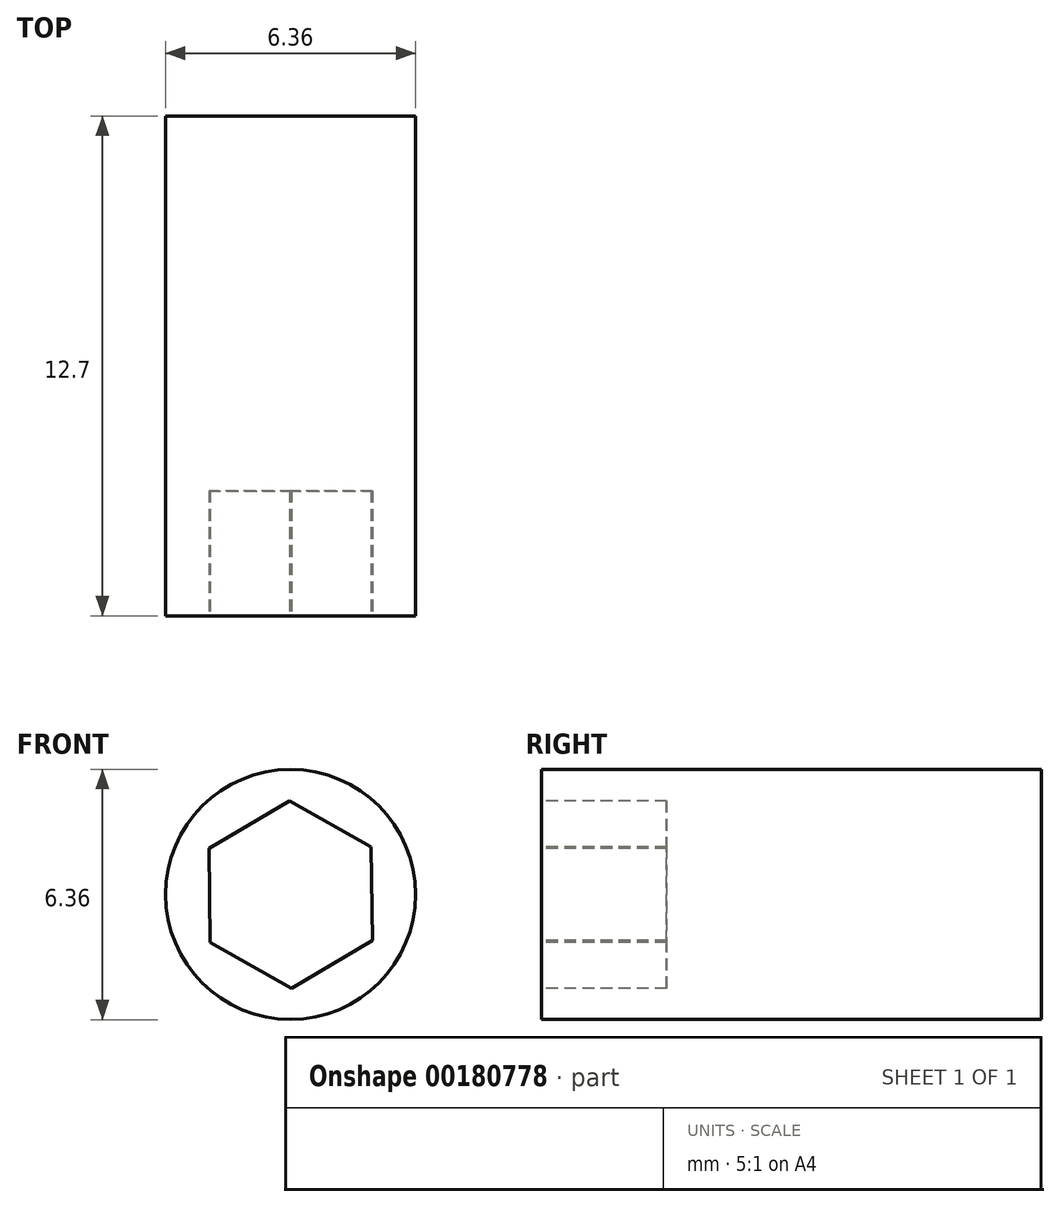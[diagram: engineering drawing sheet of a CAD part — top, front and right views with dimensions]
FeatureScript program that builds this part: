
annotation { "Feature Type Name" : "Feature", "Feature Type Description" : "" }
export const myFeature = defineFeature(function(context is Context, id is Id, definition is map)
    precondition{}
    {
        {
            var Q0;
            Q0=qCreatedBy(makeId("Front.planeOp"),FACE);
            var sketch = newSketch(context, id + "F0", { "sketchPlane" : qUnion([Q0])});
            skCircle(sketch, "E0", {"center": v(0, 0) * mm, "radius": 3.18 * mm});
            skSolve(sketch);
        }
        {
            var Q0;
            Q0 = qSketchRegion(id + "F0", true);
            extrude(context, id + "F1", {"entities" : qUnion([Q0]), "depth" : 12.7 * mm});
        }
        {
            var Q0;
            Q0=makeQuery(id+"F1.opExtrude","CAP_FACE",FACE,{"disambiguationData":[OSD([sQuery(id+"F0.wireOp",EDGE,"E0")])],"isStart":false});
            var sketch = newSketch(context, id + "F2", { "sketchPlane" : qUnion([Q0])});
            skCircle(sketch, "E1.cCircle", {"center": v(0, 0) * mm, "radius": 2.06 * mm, "construction": true});
            skLineSegment(sketch, "E1.0", {"start": v(-2.08, 1.17) * mm, "end": v(-0.03, 2.38) * mm});
            skLineSegment(sketch, "E1.1", {"start": v(-0.03, 2.38) * mm, "end": v(2.05, 1.22) * mm});
            skLineSegment(sketch, "E1.2", {"start": v(2.05, 1.22) * mm, "end": v(2.08, -1.17) * mm});
            skLineSegment(sketch, "E1.3", {"start": v(2.08, -1.17) * mm, "end": v(0.03, -2.38) * mm});
            skLineSegment(sketch, "E1.4", {"start": v(0.03, -2.38) * mm, "end": v(-2.05, -1.22) * mm});
            skLineSegment(sketch, "E1.5", {"start": v(-2.05, -1.22) * mm, "end": v(-2.08, 1.17) * mm});
            skPoint(sketch, "E1.0.midPoint", {"position": v(-1.05, 1.77) * mm});
            skSolve(sketch);
        }
        {
            var Q0;
            Q0 = qSketchRegion(id + "F2", true);
            extrude(context, id + "F3", {"entities" : qUnion([Q0]), "operationType" : NewBodyOperationType.REMOVE, "oppositeDirection" : true, "depth" : 3.17 * mm});
        }
        {
            var Q0;
            Q0 = qSketchRegion(id + "F2", true);
            extrude(context, id + "F4", {"entities" : qUnion([Q0]), "operationType" : NewBodyOperationType.REMOVE, "oppositeDirection" : true, "depth" : 2.38 * mm});
        }
    });
